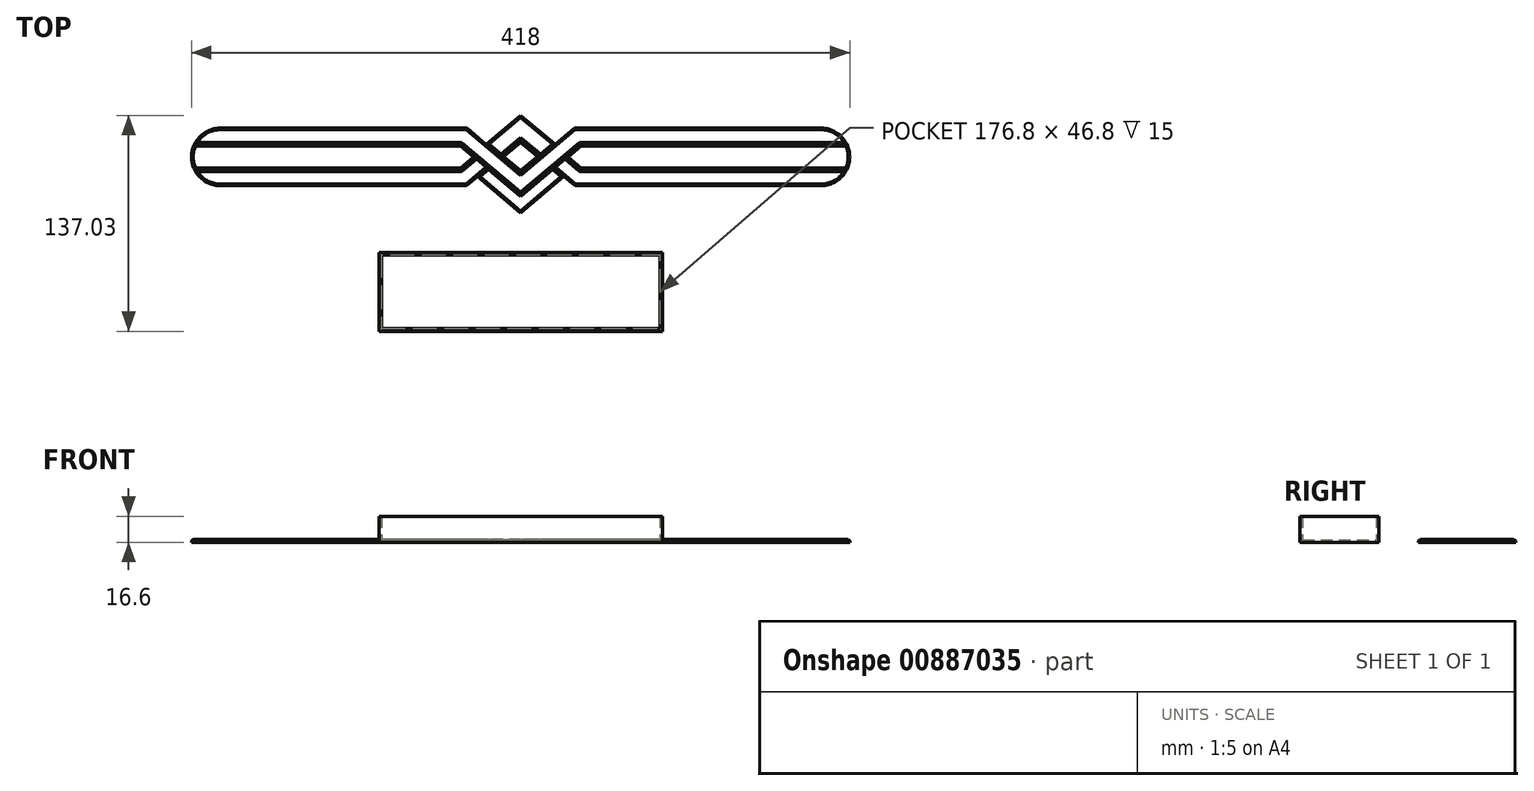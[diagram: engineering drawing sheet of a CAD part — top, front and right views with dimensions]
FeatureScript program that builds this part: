
annotation { "Feature Type Name" : "Feature", "Feature Type Description" : "" }
export const myFeature = defineFeature(function(context is Context, id is Id, definition is map)
    precondition{}
    {
        {
            var Q0;
            Q0=qCreatedBy(makeId("Top.planeOp"),FACE);
            var sketch = newSketch(context, id + "F0", { "sketchPlane" : qUnion([Q0])});
            skLineSegment(sketch, "E0", {"start": v(28.38, 0) * mm, "end": v(37.92, 8) * mm});
            skLineSegment(sketch, "E1", {"start": v(37.92, 8) * mm, "end": v(210, 8) * mm});
            skLineSegment(sketch, "E2", {"start": v(210, 8) * mm, "end": v(210, 0) * mm});
            skLineSegment(sketch, "E3.MirrorCS", {"start": v(28.38, 0) * mm, "end": v(37.92, -8) * mm});
            skLineSegment(sketch, "E4.MirrorCS", {"start": v(37.92, -8) * mm, "end": v(210, -8) * mm});
            skLineSegment(sketch, "E5.MirrorCS", {"start": v(210, -8) * mm, "end": v(210, 0) * mm});
            skLineSegment(sketch, "E6.MirrorCS", {"start": v(-28.38, 0) * mm, "end": v(-37.92, 8) * mm});
            skLineSegment(sketch, "E7.MirrorCS", {"start": v(-37.92, -8) * mm, "end": v(-210, -8) * mm});
            skLineSegment(sketch, "E8.MirrorCS", {"start": v(-28.38, 0) * mm, "end": v(-37.92, -8) * mm});
            skLineSegment(sketch, "E9.MirrorCS", {"start": v(-37.92, 8) * mm, "end": v(-210, 8) * mm});
            skLineSegment(sketch, "E10.MirrorCS", {"start": v(-210, -8) * mm, "end": v(-210, 0) * mm});
            skLineSegment(sketch, "E11.MirrorCS", {"start": v(-210, 8) * mm, "end": v(-210, 0) * mm});
            skSolve(sketch);
        }
        {
            var Q0;
            Q0=qSketchRegion(id+"F0",true);
            extrude(context, id + "F1", {"entities" : qUnion([Q0]), "depth" : 2 * mm, "offsetDistance" : 25 * mm});
        }
        {
            var Q0;
            Q0=qCreatedBy(makeId("Top.planeOp"),FACE);
            var sketch = newSketch(context, id + "F2", { "sketchPlane" : qUnion([Q0])});
            skLineSegment(sketch, "E12", {"start": v(0, -23.49) * mm, "end": v(37.82, 8.25) * mm});
            skLineSegment(sketch, "E13", {"start": v(37.82, 8.25) * mm, "end": v(210, 8.25) * mm});
            skLineSegment(sketch, "E14", {"start": v(210, 8.25) * mm, "end": v(210, 18.25) * mm});
            skLineSegment(sketch, "E15", {"start": v(210, 18.25) * mm, "end": v(34.18, 18.25) * mm});
            skLineSegment(sketch, "E16", {"start": v(34.18, 18.25) * mm, "end": v(0, -10.43) * mm});
            skLineSegment(sketch, "E17.MirrorCS", {"start": v(-210, 8.25) * mm, "end": v(-210, 18.25) * mm});
            skLineSegment(sketch, "E18.MirrorCS", {"start": v(-210, 18.25) * mm, "end": v(-34.18, 18.25) * mm});
            skLineSegment(sketch, "E19.MirrorCS", {"start": v(0, -23.49) * mm, "end": v(-37.82, 8.25) * mm});
            skLineSegment(sketch, "E20.MirrorCS", {"start": v(-34.18, 18.25) * mm, "end": v(0, -10.43) * mm});
            skLineSegment(sketch, "E21.MirrorCS", {"start": v(-37.82, 8.25) * mm, "end": v(-210, 8.25) * mm});
            skSolve(sketch);
        }
        {
            var Q0;
            Q0=qSketchRegion(id+"F2",true);
            extrude(context, id + "F3", {"entities" : qUnion([Q0]), "depth" : 2 * mm, "offsetDistance" : 25 * mm});
        }
        {
            var Q0;
            Q0=qCreatedBy(makeId("Top.planeOp"),FACE);
            var sketch = newSketch(context, id + "F4", { "sketchPlane" : qUnion([Q0])});
            skLineSegment(sketch, "E22", {"start": v(21.67, 8.08) * mm, "end": v(12.48, 0.37) * mm});
            skLineSegment(sketch, "E23", {"start": v(12.48, 0.37) * mm, "end": v(0, 10.84) * mm});
            skLineSegment(sketch, "E24", {"start": v(21.67, 8.08) * mm, "end": v(0, 26.26) * mm});
            skLineSegment(sketch, "E25", {"start": v(28.19, -0.16) * mm, "end": v(37.82, -8.25) * mm});
            skLineSegment(sketch, "E26", {"start": v(37.82, -8.25) * mm, "end": v(210, -8.25) * mm});
            skLineSegment(sketch, "E27", {"start": v(210, -8.25) * mm, "end": v(210, -18.25) * mm});
            skLineSegment(sketch, "E28", {"start": v(210, -18.25) * mm, "end": v(34.42, -18.25) * mm});
            skLineSegment(sketch, "E29", {"start": v(34.42, -18.25) * mm, "end": v(20.53, -6.6) * mm});
            skLineSegment(sketch, "E30", {"start": v(20.53, -6.6) * mm, "end": v(28.19, -0.16) * mm});
            skLineSegment(sketch, "E31.MirrorCS", {"start": v(-21.67, 8.08) * mm, "end": v(-12.48, 0.37) * mm});
            skLineSegment(sketch, "E32.MirrorCS", {"start": v(-21.67, 8.08) * mm, "end": v(0, 26.26) * mm});
            skLineSegment(sketch, "E33.MirrorCS", {"start": v(-12.48, 0.37) * mm, "end": v(0, 10.84) * mm});
            skLineSegment(sketch, "E34.MirrorCS", {"start": v(-34.42, -18.25) * mm, "end": v(-20.53, -6.6) * mm});
            skLineSegment(sketch, "E35.MirrorCS", {"start": v(-28.19, -0.16) * mm, "end": v(-37.82, -8.25) * mm});
            skLineSegment(sketch, "E36.MirrorCS", {"start": v(-210, -18.25) * mm, "end": v(-34.42, -18.25) * mm});
            skLineSegment(sketch, "E37.MirrorCS", {"start": v(-20.53, -6.6) * mm, "end": v(-28.19, -0.16) * mm});
            skLineSegment(sketch, "E38.MirrorCS", {"start": v(-37.82, -8.25) * mm, "end": v(-210, -8.25) * mm});
            skLineSegment(sketch, "E39.MirrorCS", {"start": v(-210, -8.25) * mm, "end": v(-210, -18.25) * mm});
            skSolve(sketch);
        }
        {
            var Q0;
            Q0=qSketchRegion(id+"F4",true);
            extrude(context, id + "F5", {"entities" : qUnion([Q0]), "depth" : 2 * mm, "offsetDistance" : 25 * mm});
        }
        {
            var Q0;
            Q0=qCreatedBy(makeId("Top.planeOp"),FACE);
            var sketch = newSketch(context, id + "F6", { "sketchPlane" : qUnion([Q0])});
            skLineSegment(sketch, "E40", {"start": v(0, -35.56) * mm, "end": v(27.33, -12.63) * mm});
            skLineSegment(sketch, "E41", {"start": v(27.33, -12.63) * mm, "end": v(20.33, -6.75) * mm});
            skLineSegment(sketch, "E42", {"start": v(20.33, -6.75) * mm, "end": v(0, -23.81) * mm});
            skLineSegment(sketch, "E43", {"start": v(0, -10.1) * mm, "end": v(12.29, 0.2) * mm});
            skLineSegment(sketch, "E44", {"start": v(12.29, 0.2) * mm, "end": v(0, 10.51) * mm});
            skLineSegment(sketch, "E45.MirrorCS", {"start": v(-12.29, 0.2) * mm, "end": v(0, 10.51) * mm});
            skLineSegment(sketch, "E46.MirrorCS", {"start": v(0, -35.56) * mm, "end": v(-27.33, -12.63) * mm});
            skLineSegment(sketch, "E47.MirrorCS", {"start": v(0, -10.1) * mm, "end": v(-12.29, 0.2) * mm});
            skLineSegment(sketch, "E48.MirrorCS", {"start": v(-27.33, -12.63) * mm, "end": v(-20.33, -6.75) * mm});
            skLineSegment(sketch, "E49.MirrorCS", {"start": v(-20.33, -6.75) * mm, "end": v(0, -23.81) * mm});
            skSolve(sketch);
        }
        {
            var Q0;
            Q0=qSketchRegion(id+"F6",true);
            extrude(context, id + "F7", {"entities" : qUnion([Q0]), "depth" : 2 * mm, "offsetDistance" : 25 * mm});
        }
        {
            var Q0;
            Q0=qCreatedBy(makeId("Top.planeOp"),FACE);
            var sketch = newSketch(context, id + "F8", { "sketchPlane" : qUnion([Q0])});
            skLineSegment(sketch, "E50", {"start": v(0, 26.26) * mm, "end": v(21.87, 7.92) * mm});
            skLineSegment(sketch, "E51", {"start": v(21.87, 7.92) * mm, "end": v(34.18, 18.25) * mm});
            skLineSegment(sketch, "E52", {"start": v(34.18, 18.25) * mm, "end": v(210, 18.25) * mm});
            skLineSegment(sketch, "E53", {"start": v(210, 18.25) * mm, "end": v(210, -18.25) * mm});
            skLineSegment(sketch, "E54", {"start": v(210, -18.25) * mm, "end": v(34.42, -18.25) * mm});
            skLineSegment(sketch, "E55", {"start": v(34.42, -18.25) * mm, "end": v(27.53, -12.47) * mm});
            skLineSegment(sketch, "E56", {"start": v(27.53, -12.47) * mm, "end": v(0, -35.56) * mm});
            skLineSegment(sketch, "E57.MirrorCS", {"start": v(-210, 18.25) * mm, "end": v(-210, -18.25) * mm});
            skLineSegment(sketch, "E58.MirrorCS", {"start": v(0, 26.26) * mm, "end": v(-21.87, 7.92) * mm});
            skLineSegment(sketch, "E59.MirrorCS", {"start": v(-34.18, 18.25) * mm, "end": v(-210, 18.25) * mm});
            skLineSegment(sketch, "E60.MirrorCS", {"start": v(-210, -18.25) * mm, "end": v(-34.42, -18.25) * mm});
            skLineSegment(sketch, "E61.MirrorCS", {"start": v(-34.42, -18.25) * mm, "end": v(-27.53, -12.47) * mm});
            skLineSegment(sketch, "E62.MirrorCS", {"start": v(-21.87, 7.92) * mm, "end": v(-34.18, 18.25) * mm});
            skLineSegment(sketch, "E63.MirrorCS", {"start": v(-27.53, -12.47) * mm, "end": v(0, -35.56) * mm});
            skSolve(sketch);
        }
        {
            var Q0;
            Q0=qSketchRegion(id+"F8",true);
            extrude(context, id + "F9", {"entities" : qUnion([Q0]), "depth" : 1 * mm, "offsetDistance" : 25 * mm});
        }
        {
            var Q0;
            Q0=makeQuery(id+"F1.opExtrude","SWEPT_BODY",BODY,{"disambiguationData":[OSD([sQuery(id+"F0.wireOp",EDGE,"E0"),sQuery(id+"F0.wireOp",EDGE,"E1"),sQuery(id+"F0.wireOp",EDGE,"E2"),sQuery(id+"F0.wireOp",EDGE,"E3.MirrorCS"),sQuery(id+"F0.wireOp",EDGE,"E4.MirrorCS"),sQuery(id+"F0.wireOp",EDGE,"E5.MirrorCS")])]});
            var Q1;
            Q1=makeQuery(id+"F1.opExtrude","SWEPT_BODY",BODY,{"disambiguationData":[OSD([sQuery(id+"F0.wireOp",EDGE,"E6.MirrorCS"),sQuery(id+"F0.wireOp",EDGE,"E7.MirrorCS"),sQuery(id+"F0.wireOp",EDGE,"E8.MirrorCS"),sQuery(id+"F0.wireOp",EDGE,"E9.MirrorCS"),sQuery(id+"F0.wireOp",EDGE,"E10.MirrorCS"),sQuery(id+"F0.wireOp",EDGE,"E11.MirrorCS")])]});
            var Q2;
            Q2=makeQuery(id+"F3.opExtrude","SWEPT_BODY",BODY,{"disambiguationData":[OSD([sQuery(id+"F2.wireOp",EDGE,"E12"),sQuery(id+"F2.wireOp",EDGE,"E13"),sQuery(id+"F2.wireOp",EDGE,"E14"),sQuery(id+"F2.wireOp",EDGE,"E15"),sQuery(id+"F2.wireOp",EDGE,"E16"),sQuery(id+"F2.wireOp",EDGE,"E17.MirrorCS"),sQuery(id+"F2.wireOp",EDGE,"E18.MirrorCS"),sQuery(id+"F2.wireOp",EDGE,"E19.MirrorCS"),sQuery(id+"F2.wireOp",EDGE,"E20.MirrorCS"),sQuery(id+"F2.wireOp",EDGE,"E21.MirrorCS")])]});
            var Q3;
            Q3=makeQuery(id+"F5.opExtrude","SWEPT_BODY",BODY,{"disambiguationData":[OSD([sQuery(id+"F4.wireOp",EDGE,"E22"),sQuery(id+"F4.wireOp",EDGE,"E23"),sQuery(id+"F4.wireOp",EDGE,"E24"),sQuery(id+"F4.wireOp",EDGE,"E31.MirrorCS"),sQuery(id+"F4.wireOp",EDGE,"E32.MirrorCS"),sQuery(id+"F4.wireOp",EDGE,"E33.MirrorCS")])]});
            var Q4;
            Q4=makeQuery(id+"F5.opExtrude","SWEPT_BODY",BODY,{"disambiguationData":[OSD([sQuery(id+"F4.wireOp",EDGE,"E25"),sQuery(id+"F4.wireOp",EDGE,"E26"),sQuery(id+"F4.wireOp",EDGE,"E27"),sQuery(id+"F4.wireOp",EDGE,"E28"),sQuery(id+"F4.wireOp",EDGE,"E29"),sQuery(id+"F4.wireOp",EDGE,"E30")])]});
            var Q5;
            Q5=makeQuery(id+"F5.opExtrude","SWEPT_BODY",BODY,{"disambiguationData":[OSD([sQuery(id+"F4.wireOp",EDGE,"E34.MirrorCS"),sQuery(id+"F4.wireOp",EDGE,"E35.MirrorCS"),sQuery(id+"F4.wireOp",EDGE,"E36.MirrorCS"),sQuery(id+"F4.wireOp",EDGE,"E37.MirrorCS"),sQuery(id+"F4.wireOp",EDGE,"E38.MirrorCS"),sQuery(id+"F4.wireOp",EDGE,"E39.MirrorCS")])]});
            var Q6;
            Q6=makeQuery(id+"F7.opExtrude","SWEPT_BODY",BODY,{"disambiguationData":[OSD([sQuery(id+"F6.wireOp",EDGE,"E40"),sQuery(id+"F6.wireOp",EDGE,"E41"),sQuery(id+"F6.wireOp",EDGE,"E42"),sQuery(id+"F6.wireOp",EDGE,"E46.MirrorCS"),sQuery(id+"F6.wireOp",EDGE,"E48.MirrorCS"),sQuery(id+"F6.wireOp",EDGE,"E49.MirrorCS")])]});
            var Q7;
            Q7=makeQuery(id+"F7.opExtrude","SWEPT_BODY",BODY,{"disambiguationData":[OSD([sQuery(id+"F6.wireOp",EDGE,"E43"),sQuery(id+"F6.wireOp",EDGE,"E44"),sQuery(id+"F6.wireOp",EDGE,"E45.MirrorCS"),sQuery(id+"F6.wireOp",EDGE,"E47.MirrorCS")])]});
            var Q8;
            Q8=makeQuery(id+"F9.opExtrude","SWEPT_BODY",BODY,{"disambiguationData":[OSD([sQuery(id+"F8.wireOp",EDGE,"E50"),sQuery(id+"F8.wireOp",EDGE,"E51"),sQuery(id+"F8.wireOp",EDGE,"E52"),sQuery(id+"F8.wireOp",EDGE,"E53"),sQuery(id+"F8.wireOp",EDGE,"E54"),sQuery(id+"F8.wireOp",EDGE,"E55"),sQuery(id+"F8.wireOp",EDGE,"E56"),sQuery(id+"F8.wireOp",EDGE,"E57.MirrorCS"),sQuery(id+"F8.wireOp",EDGE,"E58.MirrorCS"),sQuery(id+"F8.wireOp",EDGE,"E59.MirrorCS"),sQuery(id+"F8.wireOp",EDGE,"E60.MirrorCS"),sQuery(id+"F8.wireOp",EDGE,"E61.MirrorCS"),sQuery(id+"F8.wireOp",EDGE,"E62.MirrorCS"),sQuery(id+"F8.wireOp",EDGE,"E63.MirrorCS")])]});
            booleanBodies(context, id + "F10", {"operationType" : BooleanOperationType.UNION, "tools" : qUnion([Q0, Q1, Q2, Q3, Q4, Q5, Q6, Q7, Q8])});
        }
        {
            var Q0;
            Q0=qCreatedBy(makeId("Top.planeOp"),FACE);
            var sketch = newSketch(context, id + "F11", { "sketchPlane" : qUnion([Q0])});
            skArc(sketch, "E64", {"start": v(190.75, -18.25) * mm, "mid": v(209, 0) * mm, "end": v(190.75, 18.25) * mm});
            skLineSegment(sketch, "E65", {"start": v(190.75, 18.25) * mm, "end": v(224.62, 18.25) * mm});
            skLineSegment(sketch, "E66", {"start": v(224.62, 18.25) * mm, "end": v(224.62, -18.25) * mm});
            skLineSegment(sketch, "E67", {"start": v(190.75, -18.25) * mm, "end": v(224.62, -18.25) * mm});
            skArc(sketch, "E68.MirrorCS", {"start": v(-190.75, -18.25) * mm, "mid": v(-209, 0) * mm, "end": v(-190.75, 18.25) * mm});
            skLineSegment(sketch, "E69.MirrorCS", {"start": v(-190.75, -18.25) * mm, "end": v(-224.62, -18.25) * mm});
            skLineSegment(sketch, "E70.MirrorCS", {"start": v(-190.75, 18.25) * mm, "end": v(-224.62, 18.25) * mm});
            skLineSegment(sketch, "E71.MirrorCS", {"start": v(-224.62, 18.25) * mm, "end": v(-224.62, -18.25) * mm});
            skSolve(sketch);
        }
        {
            var Q0;
            Q0 = qSketchRegion(id + "F11", true);
            var Q1;
            Q1=makeQuery(id+"F1.opExtrude","CAP_FACE",FACE,{"disambiguationData":[OSD([sQuery(id+"F0.wireOp",EDGE,"E0"),sQuery(id+"F0.wireOp",EDGE,"E1"),sQuery(id+"F0.wireOp",EDGE,"E2"),sQuery(id+"F0.wireOp",EDGE,"E3.MirrorCS"),sQuery(id+"F0.wireOp",EDGE,"E4.MirrorCS"),sQuery(id+"F0.wireOp",EDGE,"E5.MirrorCS")])],"isStart":false});
            extrude(context, id + "F12", {"entities" : qUnion([Q0]), "operationType" : NewBodyOperationType.REMOVE, "endBound" : BoundingType.UP_TO_SURFACE, "depth" : 12.5 * mm, "endBoundEntityFace" : qUnion([Q1]), "offsetDistance" : 25 * mm});
        }
        {
            var Q0;
            Q0=makeQuery(id+"F3.opExtrude","CAP_FACE",FACE,{"disambiguationData":[OSD([sQuery(id+"F2.wireOp",EDGE,"E12"),sQuery(id+"F2.wireOp",EDGE,"E13"),sQuery(id+"F2.wireOp",EDGE,"E14"),sQuery(id+"F2.wireOp",EDGE,"E15"),sQuery(id+"F2.wireOp",EDGE,"E16"),sQuery(id+"F2.wireOp",EDGE,"E17.MirrorCS"),sQuery(id+"F2.wireOp",EDGE,"E18.MirrorCS"),sQuery(id+"F2.wireOp",EDGE,"E19.MirrorCS"),sQuery(id+"F2.wireOp",EDGE,"E20.MirrorCS"),sQuery(id+"F2.wireOp",EDGE,"E21.MirrorCS")])],"isStart":false});
            var Q1;
            Q1=makeQuery(id+"F1.opExtrude","CAP_FACE",FACE,{"disambiguationData":[OSD([sQuery(id+"F0.wireOp",EDGE,"E6.MirrorCS"),sQuery(id+"F0.wireOp",EDGE,"E7.MirrorCS"),sQuery(id+"F0.wireOp",EDGE,"E8.MirrorCS"),sQuery(id+"F0.wireOp",EDGE,"E9.MirrorCS"),sQuery(id+"F0.wireOp",EDGE,"E10.MirrorCS"),sQuery(id+"F0.wireOp",EDGE,"E11.MirrorCS")])],"isStart":false});
            var Q2;
            Q2=makeQuery(id+"F5.opExtrude","CAP_FACE",FACE,{"disambiguationData":[OSD([sQuery(id+"F4.wireOp",EDGE,"E34.MirrorCS"),sQuery(id+"F4.wireOp",EDGE,"E35.MirrorCS"),sQuery(id+"F4.wireOp",EDGE,"E36.MirrorCS"),sQuery(id+"F4.wireOp",EDGE,"E37.MirrorCS"),sQuery(id+"F4.wireOp",EDGE,"E38.MirrorCS"),sQuery(id+"F4.wireOp",EDGE,"E39.MirrorCS")])],"isStart":false});
            var Q3;
            Q3=makeQuery(id+"F5.opExtrude","CAP_FACE",FACE,{"disambiguationData":[OSD([sQuery(id+"F4.wireOp",EDGE,"E22"),sQuery(id+"F4.wireOp",EDGE,"E23"),sQuery(id+"F4.wireOp",EDGE,"E24"),sQuery(id+"F4.wireOp",EDGE,"E31.MirrorCS"),sQuery(id+"F4.wireOp",EDGE,"E32.MirrorCS"),sQuery(id+"F4.wireOp",EDGE,"E33.MirrorCS")])],"isStart":false});
            var Q4;
            Q4=makeQuery(id+"F7.opExtrude","CAP_FACE",FACE,{"disambiguationData":[OSD([sQuery(id+"F6.wireOp",EDGE,"E43"),sQuery(id+"F6.wireOp",EDGE,"E44"),sQuery(id+"F6.wireOp",EDGE,"E45.MirrorCS"),sQuery(id+"F6.wireOp",EDGE,"E47.MirrorCS")])],"isStart":false});
            var Q5;
            Q5=makeQuery(id+"F7.opExtrude","CAP_FACE",FACE,{"disambiguationData":[OSD([sQuery(id+"F6.wireOp",EDGE,"E40"),sQuery(id+"F6.wireOp",EDGE,"E41"),sQuery(id+"F6.wireOp",EDGE,"E42"),sQuery(id+"F6.wireOp",EDGE,"E46.MirrorCS"),sQuery(id+"F6.wireOp",EDGE,"E48.MirrorCS"),sQuery(id+"F6.wireOp",EDGE,"E49.MirrorCS")])],"isStart":false});
            var Q6;
            Q6=makeQuery(id+"F5.opExtrude","CAP_FACE",FACE,{"disambiguationData":[OSD([sQuery(id+"F4.wireOp",EDGE,"E25"),sQuery(id+"F4.wireOp",EDGE,"E26"),sQuery(id+"F4.wireOp",EDGE,"E27"),sQuery(id+"F4.wireOp",EDGE,"E28"),sQuery(id+"F4.wireOp",EDGE,"E29"),sQuery(id+"F4.wireOp",EDGE,"E30")])],"isStart":false});
            var Q7;
            Q7=makeQuery(id+"F1.opExtrude","CAP_FACE",FACE,{"disambiguationData":[OSD([sQuery(id+"F0.wireOp",EDGE,"E0"),sQuery(id+"F0.wireOp",EDGE,"E1"),sQuery(id+"F0.wireOp",EDGE,"E2"),sQuery(id+"F0.wireOp",EDGE,"E3.MirrorCS"),sQuery(id+"F0.wireOp",EDGE,"E4.MirrorCS"),sQuery(id+"F0.wireOp",EDGE,"E5.MirrorCS")])],"isStart":false});
            chamfer(context, id + "F13", {"entities" : qUnion([Q0, Q1, Q2, Q3, Q4, Q5, Q6, Q7]), "width" : 1 * mm, "tangentPropagation" : true});
        }
        {
            var Q0;
            Q0=qCreatedBy(makeId("Top.planeOp"),FACE);
            var sketch = newSketch(context, id + "F14", { "sketchPlane" : qUnion([Q0])});
            skLineSegment(sketch, "E72.bottom", {"start": v(90, -110.77) * mm, "end": v(-90, -110.77) * mm});
            skLineSegment(sketch, "E72.top", {"start": v(90, -60.77) * mm, "end": v(-90, -60.77) * mm});
            skLineSegment(sketch, "E72.left", {"start": v(90, -110.77) * mm, "end": v(90, -60.77) * mm});
            skLineSegment(sketch, "E72.right", {"start": v(-90, -110.77) * mm, "end": v(-90, -60.77) * mm});
            skPoint(sketch, "E72.middle", {"position": v(0, -85.77) * mm});
            skSolve(sketch);
        }
        {
            var Q0;
            Q0=makeQuery(id+"F14.imprint","IMPRINT",FACE,{"disambiguationData":[TD([[makeQuery(id+"F14.imprint","IMPRINT",EDGE,{"derivedFrom":sQuery(id+"F14.wireOp",EDGE,"E72.bottom")}),-1.0]])]});
            extrude(context, id + "F15", {"entities" : qUnion([Q0]), "depth" : 1.6 * mm, "offsetDistance" : 25 * mm});
        }
        {
            var Q0;
            Q0=makeQuery(id+"F15.opExtrude","CAP_FACE",FACE,{"disambiguationData":[OSD([sQuery(id+"F14.wireOp",EDGE,"E72.bottom"),sQuery(id+"F14.wireOp",EDGE,"E72.top"),sQuery(id+"F14.wireOp",EDGE,"E72.left"),sQuery(id+"F14.wireOp",EDGE,"E72.right")])],"isStart":false});
            var sketch = newSketch(context, id + "F16", { "sketchPlane" : qUnion([Q0])});
            skLineSegment(sketch, "E73.bottom", {"start": v(-90, -60.77) * mm, "end": v(90, -60.77) * mm});
            skLineSegment(sketch, "E73.top", {"start": v(-90, -110.77) * mm, "end": v(90, -110.77) * mm});
            skLineSegment(sketch, "E73.left", {"start": v(-90, -60.77) * mm, "end": v(-90, -110.77) * mm});
            skLineSegment(sketch, "E73.right", {"start": v(90, -60.77) * mm, "end": v(90, -110.77) * mm});
            skLineSegment(sketch, "E74.bottom", {"start": v(88.4, -109.17) * mm, "end": v(-88.4, -109.17) * mm});
            skLineSegment(sketch, "E74.top", {"start": v(88.4, -62.37) * mm, "end": v(-88.4, -62.37) * mm});
            skLineSegment(sketch, "E74.left", {"start": v(88.4, -109.17) * mm, "end": v(88.4, -62.37) * mm});
            skLineSegment(sketch, "E74.right", {"start": v(-88.4, -109.17) * mm, "end": v(-88.4, -62.37) * mm});
            skPoint(sketch, "E74.middle", {"position": v(0, -85.77) * mm});
            skPoint(sketch, "E74.middle.positionSnap0", {"position": v(90, -85.77) * mm});
            skPoint(sketch, "E74.middle.positionSnap1", {"position": v(0, -110.77) * mm});
            skPoint(sketch, "E74.centerSnap0", {"position": v(90, -85.77) * mm});
            skPoint(sketch, "E74.centerSnap1", {"position": v(0, -110.77) * mm});
            skSolve(sketch);
        }
        {
            var Q0;
            Q0 = qSketchRegion(id + "F16", true);
            extrude(context, id + "F17", {"entities" : qUnion([Q0]), "operationType" : NewBodyOperationType.ADD, "depth" : 15 * mm, "offsetDistance" : 25 * mm});
        }
    });
